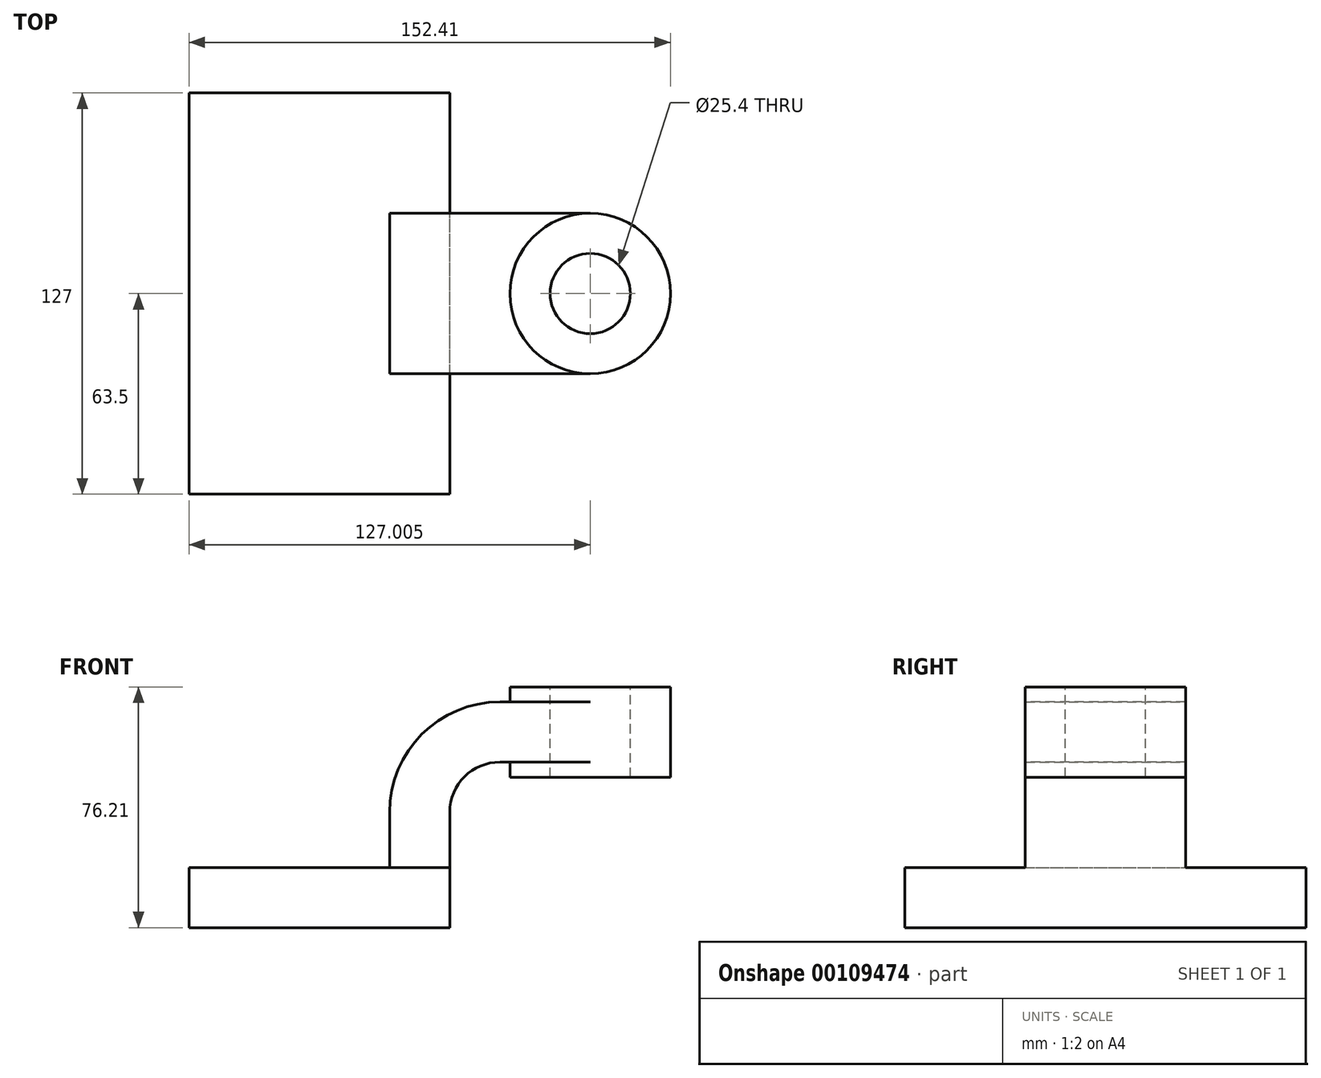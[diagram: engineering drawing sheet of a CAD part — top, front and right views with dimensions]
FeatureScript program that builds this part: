
annotation { "Feature Type Name" : "Feature", "Feature Type Description" : "" }
export const myFeature = defineFeature(function(context is Context, id is Id, definition is map)
    precondition{}
    {
        {
            var Q0;
            Q0=qCreatedBy(makeId("Front.planeOp"),FACE);
            var sketch = newSketch(context, id + "F0", { "sketchPlane" : qUnion([Q0])});
            skLineSegment(sketch, "E0.bottom", {"start": v(41.27, 9.53) * mm, "end": v(-41.28, 9.53) * mm});
            skLineSegment(sketch, "E0.top", {"start": v(41.28, -9.52) * mm, "end": v(-41.27, -9.53) * mm});
            skLineSegment(sketch, "E0.left", {"start": v(41.28, 9.53) * mm, "end": v(41.28, -9.52) * mm});
            skLineSegment(sketch, "E0.right", {"start": v(-41.28, 9.53) * mm, "end": v(-41.27, -9.53) * mm});
            skPoint(sketch, "E0.middle", {"position": v(0, 0) * mm});
            skLineSegment(sketch, "E1.bottom", {"start": v(111.12, 66.68) * mm, "end": v(60.32, 66.68) * mm});
            skLineSegment(sketch, "E1.top", {"start": v(111.12, 38.1) * mm, "end": v(60.33, 38.1) * mm});
            skLineSegment(sketch, "E1.left", {"start": v(111.12, 66.68) * mm, "end": v(111.12, 38.1) * mm});
            skLineSegment(sketch, "E1.right", {"start": v(60.32, 66.68) * mm, "end": v(60.33, 38.1) * mm});
            skPoint(sketch, "E1.middle", {"position": v(85.73, 52.39) * mm});
            skLineSegment(sketch, "E2", {"start": v(41.27, 9.53) * mm, "end": v(41.27, 27) * mm});
            skArc(sketch, "E3", {"start": v(41.28, 27) * mm, "mid": v(45.92, 38.23) * mm, "end": v(57.15, 42.88) * mm});
            skLineSegment(sketch, "E4", {"start": v(57.15, 42.88) * mm, "end": v(85.73, 42.88) * mm});
            skLineSegment(sketch, "E5.0", {"start": v(57.15, 61.93) * mm, "end": v(85.73, 61.93) * mm});
            skArc(sketch, "E5.1", {"start": v(22.23, 27) * mm, "mid": v(32.45, 51.7) * mm, "end": v(57.15, 61.93) * mm});
            skLineSegment(sketch, "E5.2", {"start": v(22.23, 9.53) * mm, "end": v(22.23, 27) * mm});
            skLineSegment(sketch, "E6", {"start": v(85.72, 66.68) * mm, "end": v(85.73, 38.1) * mm});
            skFitSpline(sketch, "E7", {"points": [v(57.15, 61.93) * mm, v(-41.28, 9.52) * mm], "startDerivative": vector(-164.46, 9.86) * mm, "endDerivative": vector(-1.38, -71.26) * mm});
            skSolve(sketch);
        }
        {
            var Q0;
            Q0=makeQuery(id+"F0.imprint","IMPRINT",FACE,{"disambiguationData":[TD([[makeQuery(id+"F0.imprint","IMPRINT",EDGE,{"derivedFrom":sQuery(id+"F0.wireOp",EDGE,"E0.top")}),-1.0]])]});
            extrude(context, id + "F1", {"entities" : qUnion([Q0]), "endBound" : BoundingType.SYMMETRIC, "depth" : 127 * mm});
        }
        {
            var Q0;
            {var subQ1=sQuery(id+"F0.wireOp",EDGE,"E2");Q0=makeQuery(id+"F0.imprint","IMPRINT",FACE,{"disambiguationData":[TD([[makeQuery(id+"F0.imprint","IMPRINT",EDGE,{"derivedFrom":subQ1}),1.0]])]});}
            var Q1;
            {var subQ0=sQuery(id+"F0.wireOp",EDGE,"E5.0");var subQ1=sQuery(id+"F0.wireOp",EDGE,"E1.right");var subQ2=makeQuery(id+"F0.imprint","INTERSECT",VERTEX,{"derivedFrom":[subQ1,subQ0]});Q1=makeQuery(id+"F0.imprint","IMPRINT",FACE,{"disambiguationData":[TD([[makeQuery(id+"F0.imprint","IMPRINT",EDGE,{"disambiguationData":[TD([[subQ2,-1.0]])],"derivedFrom":subQ1}),1.0]])]});}
            extrude(context, id + "F2", {"entities" : qUnion([Q0, Q1]), "operationType" : NewBodyOperationType.ADD, "endBound" : BoundingType.SYMMETRIC, "depth" : 50.8 * mm});
        }
        {
            var Q0;
            Q0=makeQuery(id+"F0.imprint","IMPRINT",FACE,{"disambiguationData":[TD([[makeQuery(id+"F0.imprint","IMPRINT",EDGE,{"derivedFrom":sQuery(id+"F0.wireOp",EDGE,"E5.1")}),1.0]])]});
            extrude(context, id + "F3", {"entities" : qUnion([Q0]), "operationType" : NewBodyOperationType.ADD, "endBound" : BoundingType.SYMMETRIC, "depth" : 25.4 * mm});
        }
        {
            var Q0;
            {var subQ0=sQuery(id+"F0.wireOp",EDGE,"E1.left");Q0=makeQuery(id+"F0.imprint","IMPRINT",FACE,{"disambiguationData":[TD([[makeQuery(id+"F0.imprint","IMPRINT",EDGE,{"derivedFrom":subQ0}),-1.0]])]});}
            var Q1;
            Q1=sQuery(id+"F0.wireOp",EDGE,"E6");
            revolve(context, id + "F4", {"operationType" : NewBodyOperationType.ADD, "entities" : qUnion([Q0]), "axis" : qUnion([Q1]), "revolveType" : RevolveType.FULL});
        }
        {
            var Q0;
            Q0=makeQuery(id+"F4.opRevolve","SWEPT_FACE",FACE,{"disambiguationData":[OSD([sQuery(id+"F0.wireOp",EDGE,"E1.bottom")])]});
            var sketch = newSketch(context, id + "F5", { "sketchPlane" : qUnion([Q0])});
            skPoint(sketch, "E8", {"position": v(85.73, 0) * mm});
            skSolve(sketch);
        }
        {
            var Q0;
            Q0=sQuery(id+"F5.wireOp",VERTEX,"E8");
            var Q1;
            Q1=makeQuery(id+"F1.opExtrude","SWEPT_BODY",BODY,{"disambiguationData":[OSD([sQuery(id+"F0.wireOp",EDGE,"E0.bottom"),sQuery(id+"F0.wireOp",EDGE,"E0.top"),sQuery(id+"F0.wireOp",EDGE,"E0.left"),sQuery(id+"F0.wireOp",EDGE,"E0.right")])]});
            hole(context, id + "F6", {"style" : HoleStyle.SIMPLE, "endStyle" : HoleEndStyle.THROUGH, "holeDiameter" : 25.4 * mm, "locations" : qUnion([Q0]), "scope" : qUnion([Q1]), "isTappedThrough" : true});
        }
    });
